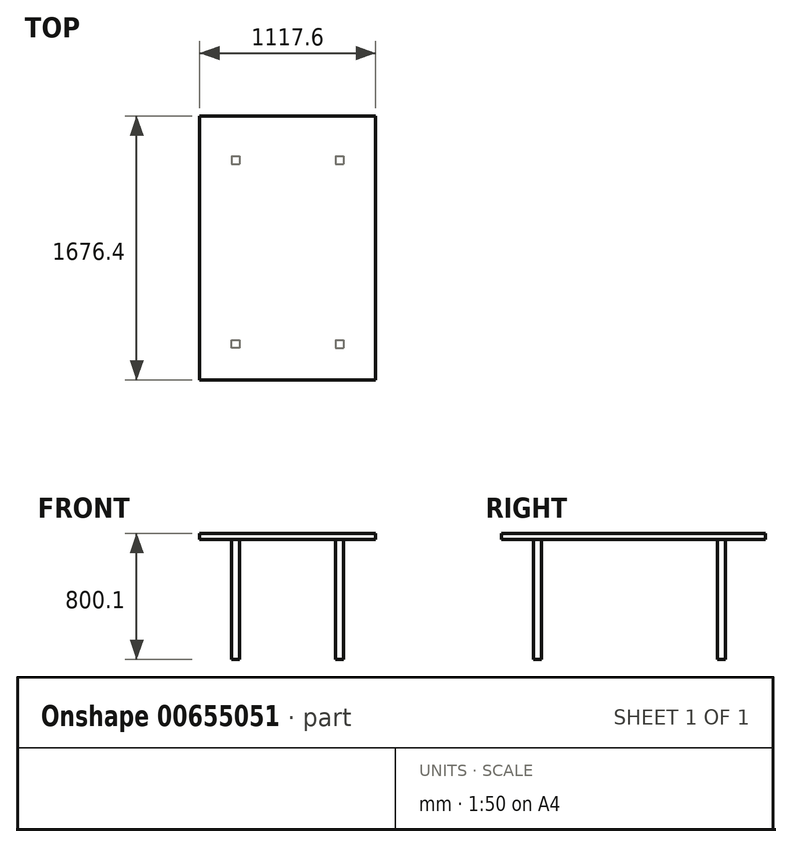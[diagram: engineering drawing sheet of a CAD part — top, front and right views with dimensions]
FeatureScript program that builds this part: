
annotation { "Feature Type Name" : "Feature", "Feature Type Description" : "" }
export const myFeature = defineFeature(function(context is Context, id is Id, definition is map)
    precondition{}
    {
        {
            var Q0;
            Q0=qCreatedBy(makeId("Top.planeOp"),FACE);
            var sketch = newSketch(context, id + "F0", { "sketchPlane" : qUnion([Q0])});
            skLineSegment(sketch, "E0.bottom", {"start": v(0, 0) * mm, "end": v(1117.6, 0) * mm});
            skLineSegment(sketch, "E0.top", {"start": v(0, -1676.4) * mm, "end": v(1117.6, -1676.4) * mm});
            skLineSegment(sketch, "E0.left", {"start": v(0, 0) * mm, "end": v(0, -1676.4) * mm});
            skLineSegment(sketch, "E0.right", {"start": v(1117.6, 0) * mm, "end": v(1117.6, -1676.4) * mm});
            skSolve(sketch);
        }
        {
            var Q0;
            Q0=makeQuery(id+"F0.imprint","IMPRINT",FACE,{"disambiguationData":[TD([[makeQuery(id+"F0.imprint","IMPRINT",EDGE,{"derivedFrom":sQuery(id+"F0.wireOp",EDGE,"E0.bottom")}),-1.0]])]});
            extrude(context, id + "F1", {"entities" : qUnion([Q0]), "depth" : 38.1 * mm, "offsetDistance" : 25.4 * mm});
        }
        {
            var Q0;
            Q0=makeQuery(id+"F1.opExtrude","CAP_FACE",FACE,{"disambiguationData":[OSD([sQuery(id+"F0.wireOp",EDGE,"E0.bottom"),sQuery(id+"F0.wireOp",EDGE,"E0.top"),sQuery(id+"F0.wireOp",EDGE,"E0.left"),sQuery(id+"F0.wireOp",EDGE,"E0.right")])],"isStart":true});
            var sketch = newSketch(context, id + "F2", { "sketchPlane" : qUnion([Q0])});
            skLineSegment(sketch, "E1", {"start": v(203.2, 1473.2) * mm, "end": v(203.2, 1422.4) * mm});
            skLineSegment(sketch, "E2", {"start": v(203.2, 1422.4) * mm, "end": v(254, 1422.4) * mm});
            skLineSegment(sketch, "E3", {"start": v(254, 1422.4) * mm, "end": v(254, 1473.2) * mm});
            skLineSegment(sketch, "E4", {"start": v(254, 1473.2) * mm, "end": v(203.2, 1473.2) * mm});
            skLineSegment(sketch, "E5.bottom", {"start": v(203.2, 254) * mm, "end": v(254, 254) * mm});
            skLineSegment(sketch, "E5.top", {"start": v(203.2, 304.8) * mm, "end": v(254, 304.8) * mm});
            skLineSegment(sketch, "E5.left", {"start": v(203.2, 254) * mm, "end": v(203.2, 304.8) * mm});
            skLineSegment(sketch, "E5.right", {"start": v(254, 254) * mm, "end": v(254, 304.8) * mm});
            skLineSegment(sketch, "E6.bottom", {"start": v(863.6, 254) * mm, "end": v(914.4, 254) * mm});
            skLineSegment(sketch, "E6.top", {"start": v(863.6, 304.8) * mm, "end": v(914.4, 304.8) * mm});
            skLineSegment(sketch, "E6.left", {"start": v(863.6, 254) * mm, "end": v(863.6, 304.8) * mm});
            skLineSegment(sketch, "E6.right", {"start": v(914.4, 254) * mm, "end": v(914.4, 304.8) * mm});
            skLineSegment(sketch, "E7.bottom", {"start": v(863.6, 1422.4) * mm, "end": v(914.4, 1422.4) * mm});
            skLineSegment(sketch, "E7.top", {"start": v(863.6, 1473.2) * mm, "end": v(914.4, 1473.2) * mm});
            skLineSegment(sketch, "E7.left", {"start": v(863.6, 1422.4) * mm, "end": v(863.6, 1473.2) * mm});
            skLineSegment(sketch, "E7.right", {"start": v(914.4, 1422.4) * mm, "end": v(914.4, 1473.2) * mm});
            skSolve(sketch);
        }
        {
            var Q0;
            Q0=makeQuery(id+"F2.imprint","IMPRINT",FACE,{"disambiguationData":[TD([[makeQuery(id+"F2.imprint","IMPRINT",EDGE,{"derivedFrom":sQuery(id+"F2.wireOp",EDGE,"E1")}),1.0]])]});
            var Q1;
            Q1=makeQuery(id+"F2.imprint","IMPRINT",FACE,{"disambiguationData":[TD([[makeQuery(id+"F2.imprint","IMPRINT",EDGE,{"derivedFrom":sQuery(id+"F2.wireOp",EDGE,"E7.bottom")}),1.0]])]});
            var Q2;
            Q2=makeQuery(id+"F2.imprint","IMPRINT",FACE,{"disambiguationData":[TD([[makeQuery(id+"F2.imprint","IMPRINT",EDGE,{"derivedFrom":sQuery(id+"F2.wireOp",EDGE,"E6.bottom")}),1.0]])]});
            var Q3;
            Q3=makeQuery(id+"F2.imprint","IMPRINT",FACE,{"disambiguationData":[TD([[makeQuery(id+"F2.imprint","IMPRINT",EDGE,{"derivedFrom":sQuery(id+"F2.wireOp",EDGE,"E5.bottom")}),1.0]])]});
            extrude(context, id + "F3", {"entities" : qUnion([Q0, Q1, Q2, Q3]), "operationType" : NewBodyOperationType.ADD, "depth" : 762 * mm, "offsetDistance" : 25.4 * mm});
        }
    });
